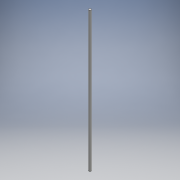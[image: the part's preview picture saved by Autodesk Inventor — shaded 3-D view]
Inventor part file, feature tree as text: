
AUTODESK INVENTOR PART (.ipt)
format: ipt  version: 2016 SP1 (Build 200210100, 210)  size: 83,968 bytes
history: native  units: mm
features: extrude x1, sketch x1
ambient origin geometry x8: Origin, YZ Plane, XZ Plane, XY Plane, X Axis, Y Axis, Z Axis, Center Point
bodies: Solid1 (feature_tree)
feature tree (2):
  extrude  "Extrusion1"  Depth=300.0mm TaperAngle=0.0deg
  sketch  "Sketch1"  dims[d0=5.0mm d1=300.0mm d2=0.0mm]
